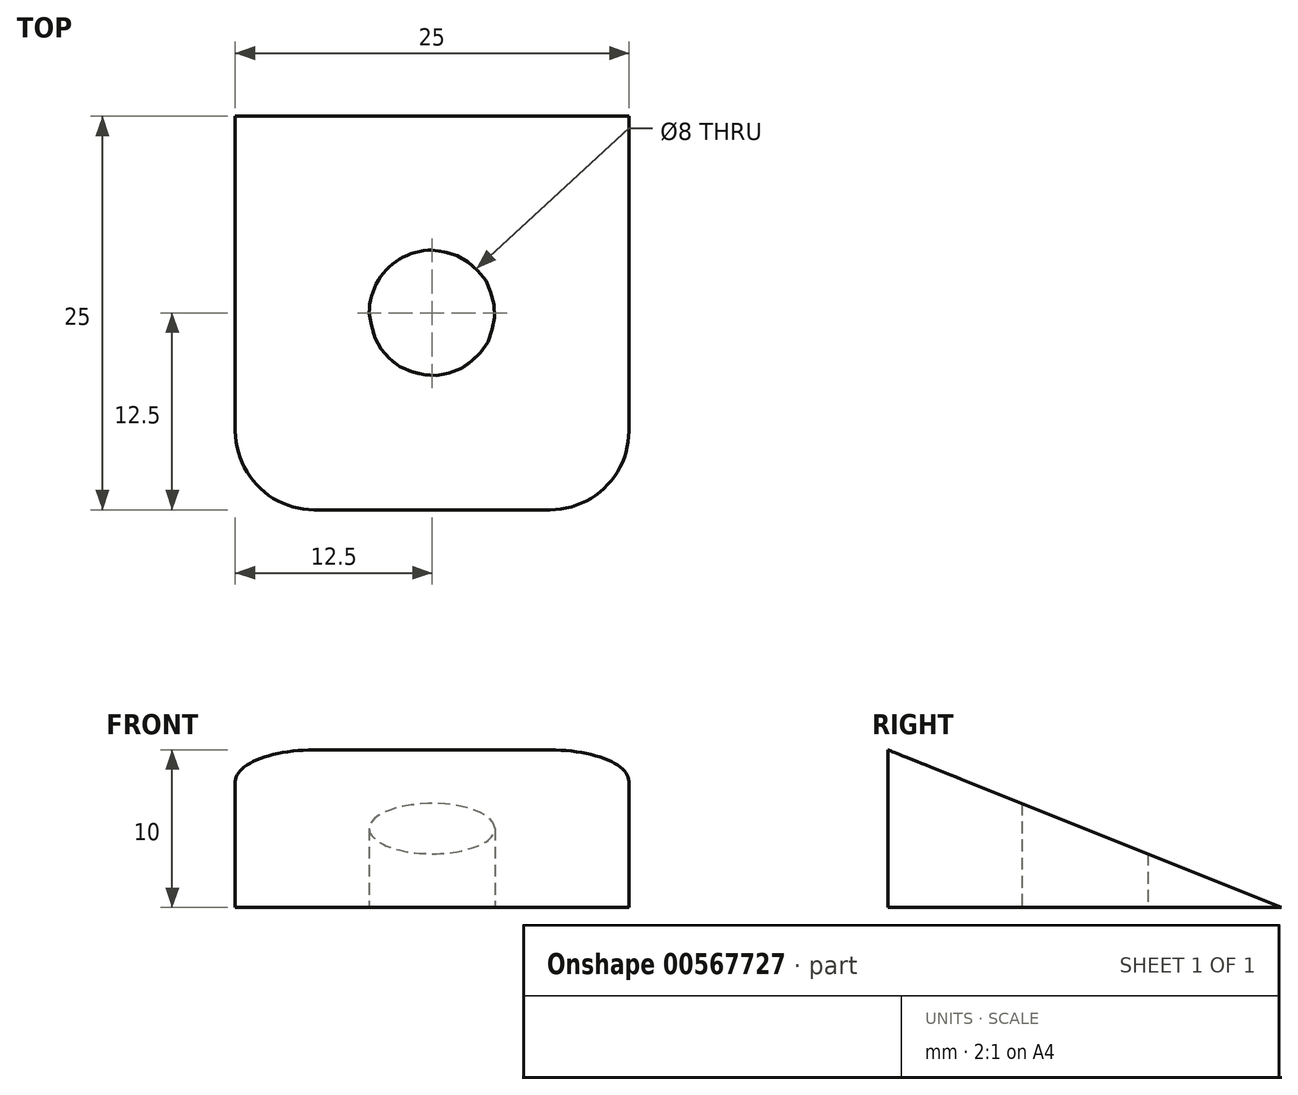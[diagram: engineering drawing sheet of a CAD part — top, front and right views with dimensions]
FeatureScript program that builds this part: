
annotation { "Feature Type Name" : "Feature", "Feature Type Description" : "" }
export const myFeature = defineFeature(function(context is Context, id is Id, definition is map)
    precondition{}
    {
        {
            var Q0;
            Q0=qCreatedBy(makeId("Top.planeOp"),FACE);
            var sketch = newSketch(context, id + "F0", { "sketchPlane" : qUnion([Q0])});
            skLineSegment(sketch, "E0.bottom", {"start": v(-12.5, 12.5) * mm, "end": v(12.5, 12.5) * mm});
            skLineSegment(sketch, "E0.top", {"start": v(-12.5, -12.5) * mm, "end": v(12.5, -12.5) * mm});
            skLineSegment(sketch, "E0.left", {"start": v(-12.5, 12.5) * mm, "end": v(-12.5, -12.5) * mm});
            skLineSegment(sketch, "E0.right", {"start": v(12.5, 12.5) * mm, "end": v(12.5, -12.5) * mm});
            skPoint(sketch, "E0.middle", {"position": v(0, 0) * mm});
            skSolve(sketch);
        }
        {
            var Q0;
            Q0 = qSketchRegion(id + "F0", true);
            extrude(context, id + "F1", {"entities" : qUnion([Q0]), "depth" : 10 * mm, "offsetDistance" : 25 * mm});
        }
        {
            var Q0;
            Q0=makeQuery(id+"F1.opExtrude","SWEPT_FACE",FACE,{"disambiguationData":[OSD([sQuery(id+"F0.wireOp",EDGE,"E0.right")])]});
            var sketch = newSketch(context, id + "F2", { "sketchPlane" : qUnion([Q0])});
            skLineSegment(sketch, "E1", {"start": v(-12.5, 10) * mm, "end": v(12.5, 0) * mm});
            skSolve(sketch);
        }
        {
            var Q0;
            Q0=makeQuery(id+"F2.imprint","IMPRINT",FACE,{"disambiguationData":[TD([[makeQuery(id+"F2.imprint","IMPRINT",EDGE,{"derivedFrom":sQuery(id+"F2.wireOp",EDGE,"E1")}),1.0]])]});
            extrude(context, id + "F3", {"entities" : qUnion([Q0]), "operationType" : NewBodyOperationType.REMOVE, "oppositeDirection" : true, "depth" : 25 * mm, "offsetDistance" : 25 * mm});
        }
        {
            var Q0;
            Q0=makeQuery(id+"F1.opExtrude","CAP_FACE",FACE,{"disambiguationData":[OSD([sQuery(id+"F0.wireOp",EDGE,"E0.bottom"),sQuery(id+"F0.wireOp",EDGE,"E0.top"),sQuery(id+"F0.wireOp",EDGE,"E0.left"),sQuery(id+"F0.wireOp",EDGE,"E0.right")])],"isStart":true});
            var sketch = newSketch(context, id + "F4", { "sketchPlane" : qUnion([Q0])});
            skPoint(sketch, "E2", {"position": v(0, 0) * mm});
            skSolve(sketch);
        }
        {
            var Q0;
            Q0=sQuery(id+"F4.wireOp",VERTEX,"E2");
            var Q1;
            Q1=makeQuery(id+"F1.opExtrude","SWEPT_BODY",BODY,{"disambiguationData":[OSD([sQuery(id+"F0.wireOp",EDGE,"E0.bottom"),sQuery(id+"F0.wireOp",EDGE,"E0.top"),sQuery(id+"F0.wireOp",EDGE,"E0.left"),sQuery(id+"F0.wireOp",EDGE,"E0.right")])]});
            hole(context, id + "F5", {"style" : HoleStyle.SIMPLE, "endStyle" : HoleEndStyle.BLIND, "holeDiameter" : 8 * mm, "holeDepth" : 30 * mm, "isTappedThrough" : true, "tappedDepth" : 12 * mm, "tapClearance" : 3, "startFromSketch" : true, "locations" : qUnion([Q0]), "scope" : qUnion([Q1])});
        }
        {
            var Q0;
            Q0=makeQuery(id+"F1.opExtrude","SWEPT_EDGE",EDGE,{"disambiguationData":[OSD([sQuery(id+"F0.wireOp",EDGE,"E0.top"),sQuery(id+"F0.wireOp",EDGE,"E0.right")])]});
            var Q1;
            Q1=makeQuery(id+"F1.opExtrude","SWEPT_EDGE",EDGE,{"disambiguationData":[OSD([sQuery(id+"F0.wireOp",EDGE,"E0.top"),sQuery(id+"F0.wireOp",EDGE,"E0.left")])]});
            fillet(context, id + "F6", {"entities" : qUnion([Q0, Q1]), "radius" : 5 * mm, "tangentPropagation" : true, "allowEdgeOverflow" : false});
        }
    });
